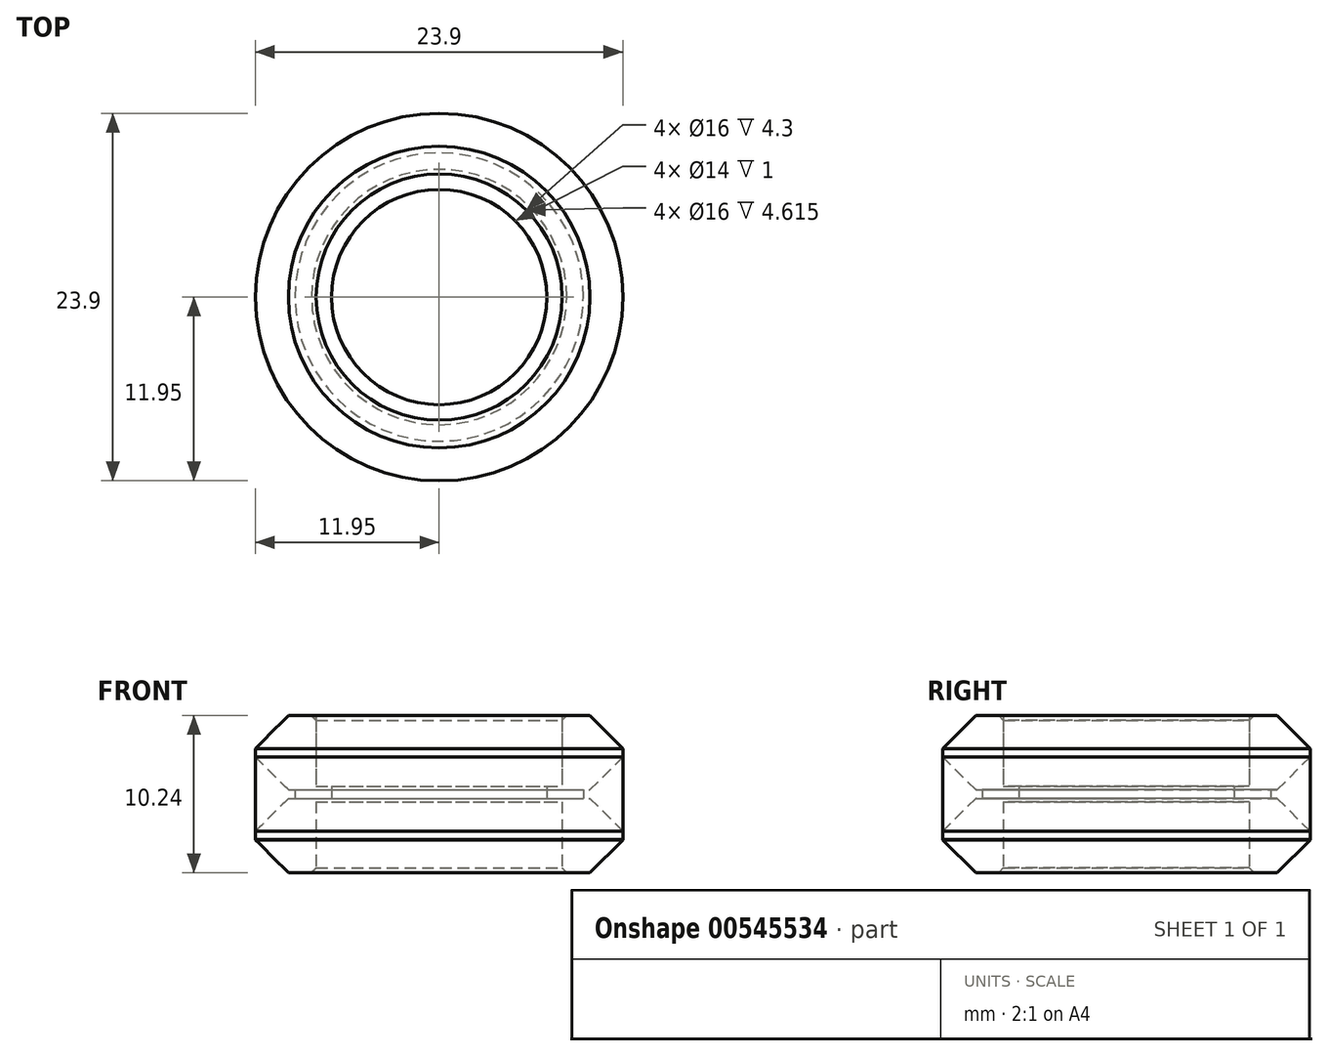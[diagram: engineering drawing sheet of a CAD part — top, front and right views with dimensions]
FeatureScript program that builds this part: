
annotation { "Feature Type Name" : "Feature", "Feature Type Description" : "" }
export const myFeature = defineFeature(function(context is Context, id is Id, definition is map)
    precondition{}
    {
        {
            var Q0;
            Q0=qCreatedBy(makeId("Front.planeOp"),FACE);
            var sketch = newSketch(context, id + "F0", { "sketchPlane" : qUnion([Q0])});
            skLineSegment(sketch, "E0", {"start": v(-8, 5.12) * mm, "end": v(-9.8, 5.12) * mm});
            skLineSegment(sketch, "E1", {"start": v(-9.8, 5.12) * mm, "end": v(-11.95, 2.97) * mm});
            skLineSegment(sketch, "E2", {"start": v(-11.95, 2.97) * mm, "end": v(-11.95, 2.42) * mm});
            skLineSegment(sketch, "E3", {"start": v(-11.95, -2.97) * mm, "end": v(-9.8, -5.11) * mm});
            skLineSegment(sketch, "E4", {"start": v(-9.8, -5.12) * mm, "end": v(-8, -5.12) * mm});
            skLineSegment(sketch, "E5", {"start": v(0, -5.12) * mm, "end": v(0, 5.12) * mm, "construction": true});
            skLineSegment(sketch, "E6", {"start": v(0, 0) * mm, "end": v(-9.47, 0) * mm, "construction": true});
            skLineSegment(sketch, "E7", {"start": v(-8, 5.12) * mm, "end": v(-8, 0.5) * mm});
            skLineSegment(sketch, "E8", {"start": v(-8, 0.5) * mm, "end": v(-7, 0.5) * mm});
            skLineSegment(sketch, "E9", {"start": v(-7, 0.5) * mm, "end": v(-7, -0.5) * mm});
            skLineSegment(sketch, "E10", {"start": v(-7, -0.5) * mm, "end": v(-8, -0.5) * mm});
            skLineSegment(sketch, "E11", {"start": v(-8, -0.5) * mm, "end": v(-8, -5.12) * mm});
            skLineSegment(sketch, "E12", {"start": v(-11.95, -2.42) * mm, "end": v(-11.95, -2.97) * mm});
            skLineSegment(sketch, "E13", {"start": v(-9.8, -0.27) * mm, "end": v(-11.95, -2.42) * mm});
            skLineSegment(sketch, "E14", {"start": v(-11.95, 2.42) * mm, "end": v(-9.8, 0.28) * mm});
            skLineSegment(sketch, "E15", {"start": v(-9.8, -0.27) * mm, "end": v(-9.38, -0.27) * mm});
            skLineSegment(sketch, "E16", {"start": v(-9.38, -0.27) * mm, "end": v(-9.38, 0.28) * mm});
            skLineSegment(sketch, "E17", {"start": v(-9.38, 0.28) * mm, "end": v(-9.8, 0.28) * mm});
            skSolve(sketch);
        }
        {
            var Q0;
            Q0=qCreatedBy(makeId("Front.planeOp"),FACE);
            var sketch = newSketch(context, id + "F1", { "sketchPlane" : qUnion([Q0])});
            skLineSegment(sketch, "E18", {"start": v(-8.3, 5.1) * mm, "end": v(-9.8, 5.1) * mm});
            skLineSegment(sketch, "E19", {"start": v(-9.8, 5.1) * mm, "end": v(-11.95, 2.95) * mm});
            skLineSegment(sketch, "E20", {"start": v(-11.95, 2.95) * mm, "end": v(-11.95, -2.95) * mm});
            skLineSegment(sketch, "E21", {"start": v(-11.95, -2.95) * mm, "end": v(-9.8, -5.1) * mm});
            skLineSegment(sketch, "E22", {"start": v(-9.8, -5.1) * mm, "end": v(-8.3, -5.1) * mm});
            skLineSegment(sketch, "E23", {"start": v(0, -5.1) * mm, "end": v(0, 5.1) * mm, "construction": true});
            skLineSegment(sketch, "E24", {"start": v(0, 0) * mm, "end": v(-5.4, 0) * mm, "construction": true});
            skLineSegment(sketch, "E25", {"start": v(-8, 4.8) * mm, "end": v(-8, 0.5) * mm});
            skLineSegment(sketch, "E26", {"start": v(-8, 0.5) * mm, "end": v(-7, 0.5) * mm});
            skLineSegment(sketch, "E27", {"start": v(-7, 0.5) * mm, "end": v(-7, -0.5) * mm});
            skLineSegment(sketch, "E28", {"start": v(-7, -0.5) * mm, "end": v(-8, -0.5) * mm});
            skLineSegment(sketch, "E29", {"start": v(-8, -0.5) * mm, "end": v(-8, -5.1) * mm});
            skLineSegment(sketch, "E30", {"start": v(-8.3, 5.1) * mm, "end": v(-8, 4.8) * mm});
            skLineSegment(sketch, "E31.MirrorCS", {"start": v(-8.3, -5.1) * mm, "end": v(-8, -4.8) * mm});
            skSolve(sketch);
        }
        {
            var Q0;
            Q0 = qSketchRegion(id + "F1", true);
            var Q1;
            Q1=sQuery(id+"F1.wireOp",EDGE,"E23");
            revolve(context, id + "F2", {"entities" : qUnion([Q0]), "axis" : qUnion([Q1]), "revolveType" : RevolveType.FULL});
        }
        {
            var Q0;
            Q0=makeQuery(id+"F0.imprint","IMPRINT",FACE,{"disambiguationData":[TD([[makeQuery(id+"F0.imprint","IMPRINT",EDGE,{"derivedFrom":sQuery(id+"F0.wireOp",EDGE,"E0")}),1.0]])]});
            var Q1;
            Q1=sQuery(id+"F0.wireOp",EDGE,"E5");
            revolve(context, id + "F3", {"entities" : qUnion([Q0]), "axis" : qUnion([Q1]), "revolveType" : RevolveType.FULL});
        }
        {
            var Q0;
            Q0=makeQuery(id+"F0.imprint","IMPRINT",FACE,{"disambiguationData":[TD([[makeQuery(id+"F0.imprint","IMPRINT",EDGE,{"derivedFrom":sQuery(id+"F0.wireOp",EDGE,"E0")}),1.0]])]});
            var Q1;
            Q1=sQuery(id+"F0.wireOp",EDGE,"E5");
            revolve(context, id + "F4", {"entities" : qUnion([Q0]), "axis" : qUnion([Q1]), "revolveType" : RevolveType.FULL});
        }
        {
            var Q0;
            Q0=makeQuery(id+"F1.imprint","IMPRINT",FACE,{"disambiguationData":[TD([[makeQuery(id+"F1.imprint","IMPRINT",EDGE,{"derivedFrom":sQuery(id+"F1.wireOp",EDGE,"E18")}),1.0]])]});
            var Q1;
            Q1=sQuery(id+"F1.wireOp",EDGE,"E23");
            revolve(context, id + "F5", {"entities" : qUnion([Q0]), "axis" : qUnion([Q1]), "revolveType" : RevolveType.FULL});
        }
        {
            var Q0;
            Q0=qCreatedBy(makeId("Front.planeOp"),FACE);
            cPlane(context, id + "F6", {"entities" : qUnion([Q0]), "cplaneType" : CPlaneType.OFFSET, "offset" : (23.9 / 2) * mm, "width" : 150 * mm, "height" : 150 * mm});
        }
        {
            var Q0;
            Q0=qCreatedBy(id+"F6.planeOp",FACE);
            var sketch = newSketch(context, id + "F7", { "sketchPlane" : qUnion([Q0])});
            skLineSegment(sketch, "E32.0", {"start": v(11.95, 2.95) * mm, "end": v(-11.95, 2.95) * mm, "construction": true});
            skLineSegment(sketch, "E32.1", {"start": v(11.95, -2.95) * mm, "end": v(-11.95, -2.95) * mm, "construction": true});
            skLineSegment(sketch, "E33", {"start": v(11.95, -2.95) * mm, "end": v(-11.95, 2.95) * mm, "construction": true});
            skSolve(sketch);
        }
    });
